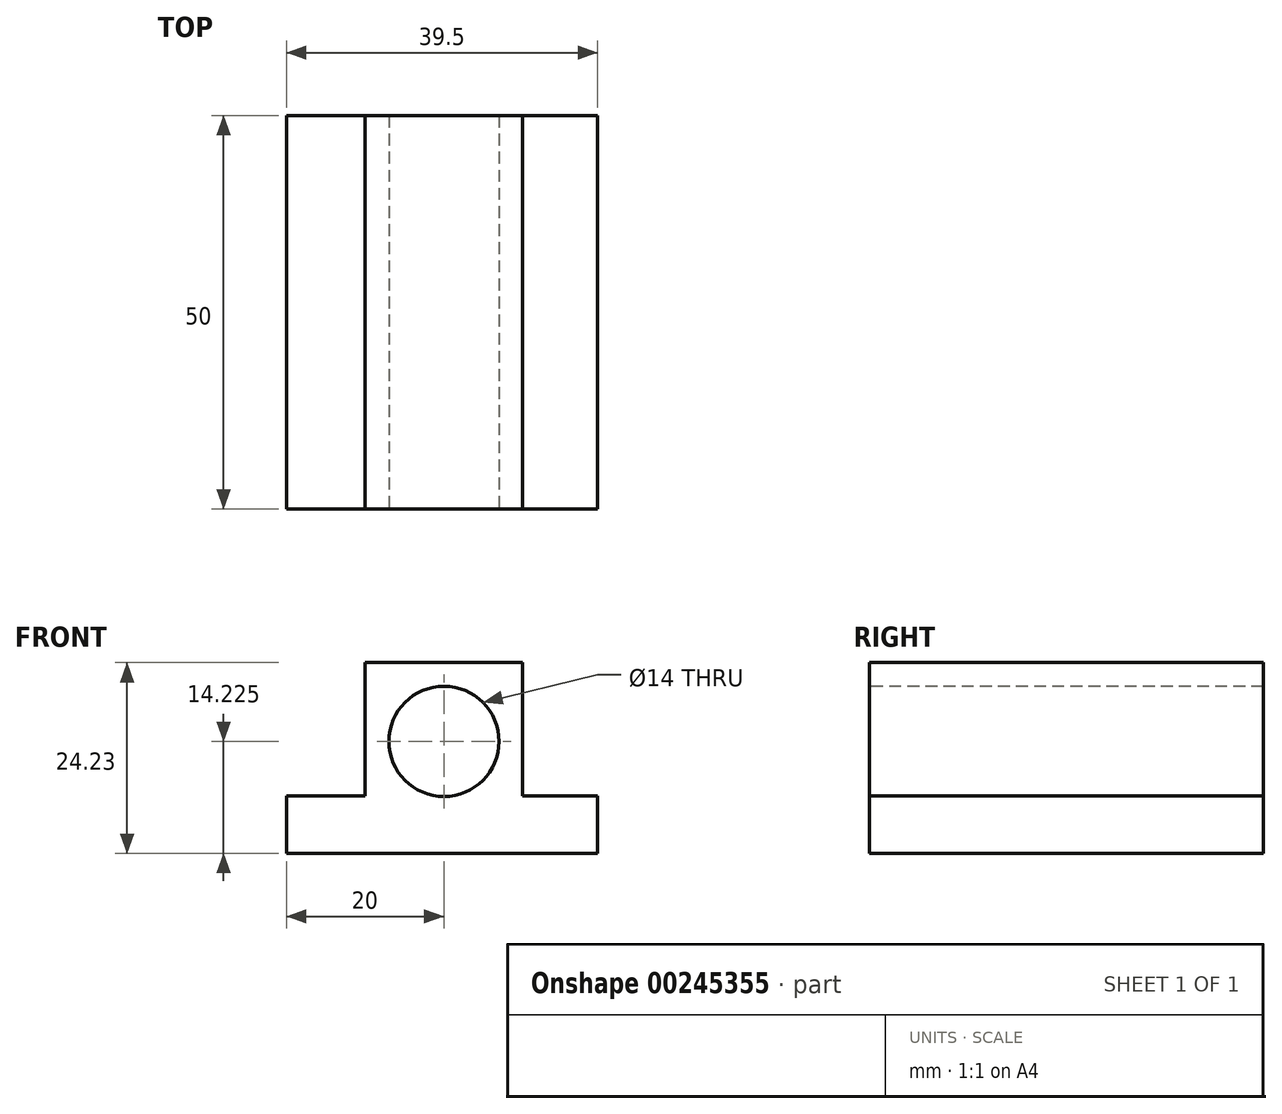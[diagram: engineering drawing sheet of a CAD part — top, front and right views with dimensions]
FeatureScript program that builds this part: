
annotation { "Feature Type Name" : "Feature", "Feature Type Description" : "" }
export const myFeature = defineFeature(function(context is Context, id is Id, definition is map)
    precondition{}
    {
        {
            var Q0;
            Q0=qCreatedBy(makeId("Front.planeOp"),FACE);
            var sketch = newSketch(context, id + "F0", { "sketchPlane" : qUnion([Q0])});
            skLineSegment(sketch, "E0", {"start": v(0, 0) * mm, "end": v(39.5, 0) * mm});
            skLineSegment(sketch, "E1", {"start": v(39.5, 0) * mm, "end": v(39.5, 7.3) * mm});
            skLineSegment(sketch, "E2", {"start": v(39.5, 7.3) * mm, "end": v(30, 7.3) * mm});
            skLineSegment(sketch, "E3", {"start": v(30, 7.3) * mm, "end": v(30, 24.23) * mm});
            skLineSegment(sketch, "E4", {"start": v(30, 24.23) * mm, "end": v(10, 24.23) * mm});
            skLineSegment(sketch, "E5", {"start": v(10, 24.23) * mm, "end": v(10, 7.3) * mm});
            skLineSegment(sketch, "E6", {"start": v(10, 7.3) * mm, "end": v(0, 7.3) * mm});
            skLineSegment(sketch, "E7", {"start": v(0, 7.3) * mm, "end": v(0, 0) * mm});
            skSolve(sketch);
        }
        {
            var Q0;
            Q0=makeQuery(id+"F0.imprint","IMPRINT",FACE,{"disambiguationData":[TD([[makeQuery(id+"F0.imprint","IMPRINT",EDGE,{"derivedFrom":sQuery(id+"F0.wireOp",EDGE,"E0")}),1.0]])]});
            extrude(context, id + "F1", {"entities" : qUnion([Q0]), "depth" : 50 * mm});
        }
        {
            var Q0;
            Q0=makeQuery(id+"F1.opExtrude","CAP_FACE",FACE,{"disambiguationData":[OSD([sQuery(id+"F0.wireOp",EDGE,"E0"),sQuery(id+"F0.wireOp",EDGE,"E1"),sQuery(id+"F0.wireOp",EDGE,"E2"),sQuery(id+"F0.wireOp",EDGE,"E3"),sQuery(id+"F0.wireOp",EDGE,"E4"),sQuery(id+"F0.wireOp",EDGE,"E5"),sQuery(id+"F0.wireOp",EDGE,"E6"),sQuery(id+"F0.wireOp",EDGE,"E7")])],"isStart":false});
            var sketch = newSketch(context, id + "F2", { "sketchPlane" : qUnion([Q0])});
            skPoint(sketch, "E8", {"position": v(20, 14.23) * mm});
            skSolve(sketch);
        }
        {
            var Q0;
            Q0=sQuery(id+"F2.wireOp",VERTEX,"E8");
            var Q1;
            Q1=makeQuery(id+"F1.opExtrude","SWEPT_BODY",BODY,{"disambiguationData":[OSD([sQuery(id+"F0.wireOp",EDGE,"E0"),sQuery(id+"F0.wireOp",EDGE,"E1"),sQuery(id+"F0.wireOp",EDGE,"E2"),sQuery(id+"F0.wireOp",EDGE,"E3"),sQuery(id+"F0.wireOp",EDGE,"E4"),sQuery(id+"F0.wireOp",EDGE,"E5"),sQuery(id+"F0.wireOp",EDGE,"E6"),sQuery(id+"F0.wireOp",EDGE,"E7")])]});
            hole(context, id + "F3", {"style" : HoleStyle.SIMPLE, "endStyle" : HoleEndStyle.THROUGH, "standardTappedOrClearance" : lookupTablePath({ "standard" : "ISO", "engagement" : "75%", "pitch" : "2 mm", "size" : "M16", "type" : "Tapped" }), "standardBlindInLast" : lookupTablePath({ "standard" : "ISO", "engagement" : "75%", "pitch" : "2 mm", "size" : "M16", "type" : "Tapped" }), "holeDiameter" : 14 * mm, "showTappedDepth" : true, "tappedDepth" : 12 * mm, "tapClearance" : 3, "locations" : qUnion([Q0]), "scope" : qUnion([Q1]), "majorDiameter" : 16 * mm});
        }
    });
